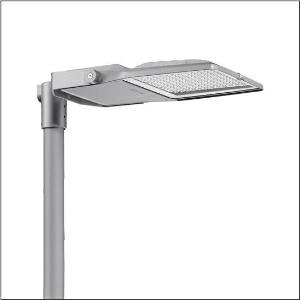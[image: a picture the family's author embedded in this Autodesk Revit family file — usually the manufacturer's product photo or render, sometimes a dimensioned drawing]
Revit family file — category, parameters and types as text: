
# Revit family: floodlight_fl_21_iq_midi___pl52_5xa7781e2d3a_77a1
name_source: partatom
category: Lighting Fixtures
units: mm (PartAtom-declared; Revit-internal decimal feet)

## family parameters
Cut with Voids When Loaded = No
Host = Face
Light Source = No
Part Type = Normal
Room Calculation Point = No
Round Connector Dimension = Use Diameter
Shared = No

## types (1)
- --- (1 x LED, 26850 lm, 208.1 W, 3000K)
    Apparent Load = 208 VA
    CIE Flux Codes = 26 60 98 100 100
    Color Rendering = 70
    Color Temperature = 3000K
    Default Elevation = 1800 mm
    Description = Floodlight FL 21 iQ midi, floodlight, primary light control with lens, of PMMA, primary optical cover: protective disc, of toughened safety glass, transparent, light distribution: PL52, light emission: direct distribution, installation type: surface-mounted, LED, High Power LED, rated luminous flux: 26.850lm, luminous efficacy: 129lm/W, light colour: 730, colour temperature: 3000K, control gear: ECG iQ, control: optimised constant luminous flux control (CLO 2.0), Desk-Remote (wireless, voltage-free reading and setting of iQ features in the workshop via application-optimized NFC function/RFID function), Light-Fading, Smart-Wire, Night-Set, Lumen-Switch, Temp-Guard, Auto-Match, with terminal, 6-pole, mains connection: 220..240V, AC, 50/60Hz, start of lifetime: 208W, end of service life: 227W, reduction: 90W, luminaire housing, of diecast aluminium, powder-coated, Siteco® metallic grey (DB 702S), corrosivity category C5 mid according to DIN EN ISO 12944, sealing non-destructively replaceable, please order mast flange separately, mast bracket, of steel, galvanised, powder-coated, Siteco® metallic grey (DB 702S), protection rating (complete): IP66, insulation class (complete): insulation class II (safety insulation), certification: CE, protection symbol: D, impact resistance: IK08, permissible operating ambient temperature: -40..+40°C, permissible operating ambient temperature for outdoor applications: -40..+50°C, standard: DIN EN 12944, LABS conformity tested according to VDMA 24364:2018-05, packaging unit: 1 piece

Light Distribution: PL52
    Height = 76 mm
    Lamp = 1 x LED
    Lamp Light Flux = 26850 lm
    Lamp Power = 208.1 W
    Lamp count = 1
    Length = 657 mm
    Luminous efficacy = 129 lm/W
    Manufacturer = Siteco
    ModVariant = No
    Model = 5XA7781E2D3A
    Number of Poles = 1
    OnlyDefault = Yes
    Power Factor = 1
    Product Name = Floodlight FL 21 iQ midi | PL52
    Product group = floodlight | pylon annexe
    ProductGroupID = 6200
    Protection Class = Protection class II
    Protection Degree = IP 66
    RLX_Detail_Level = 1
    RLX_Emergency_Light_Flux = 0 lm
    RLX_Emergency_Type = 0
    RLX_Emergency_Type_DB = No
    RlxData = <blob elided: 153933 chars, md5=00544517>
    Socket = socket
    Standby Power = 0 W
    System Light Flux = 26850 lm
    System Power = 208 W
    Type Comments = factory setting: luminous flux: 100 % | dim-lin: 254 | 710 mA
    Type Image = l_1007123.jpg
    URL = http://relux.com
    VarID = @adj_036403
    Voltage = 0 V
    Weight = 0.00 kg
    Width = 442 mm

## geometry (parser evidence)
native form markers: Blend x4, Sweep x15
no freeform markers — native parametric forms only
